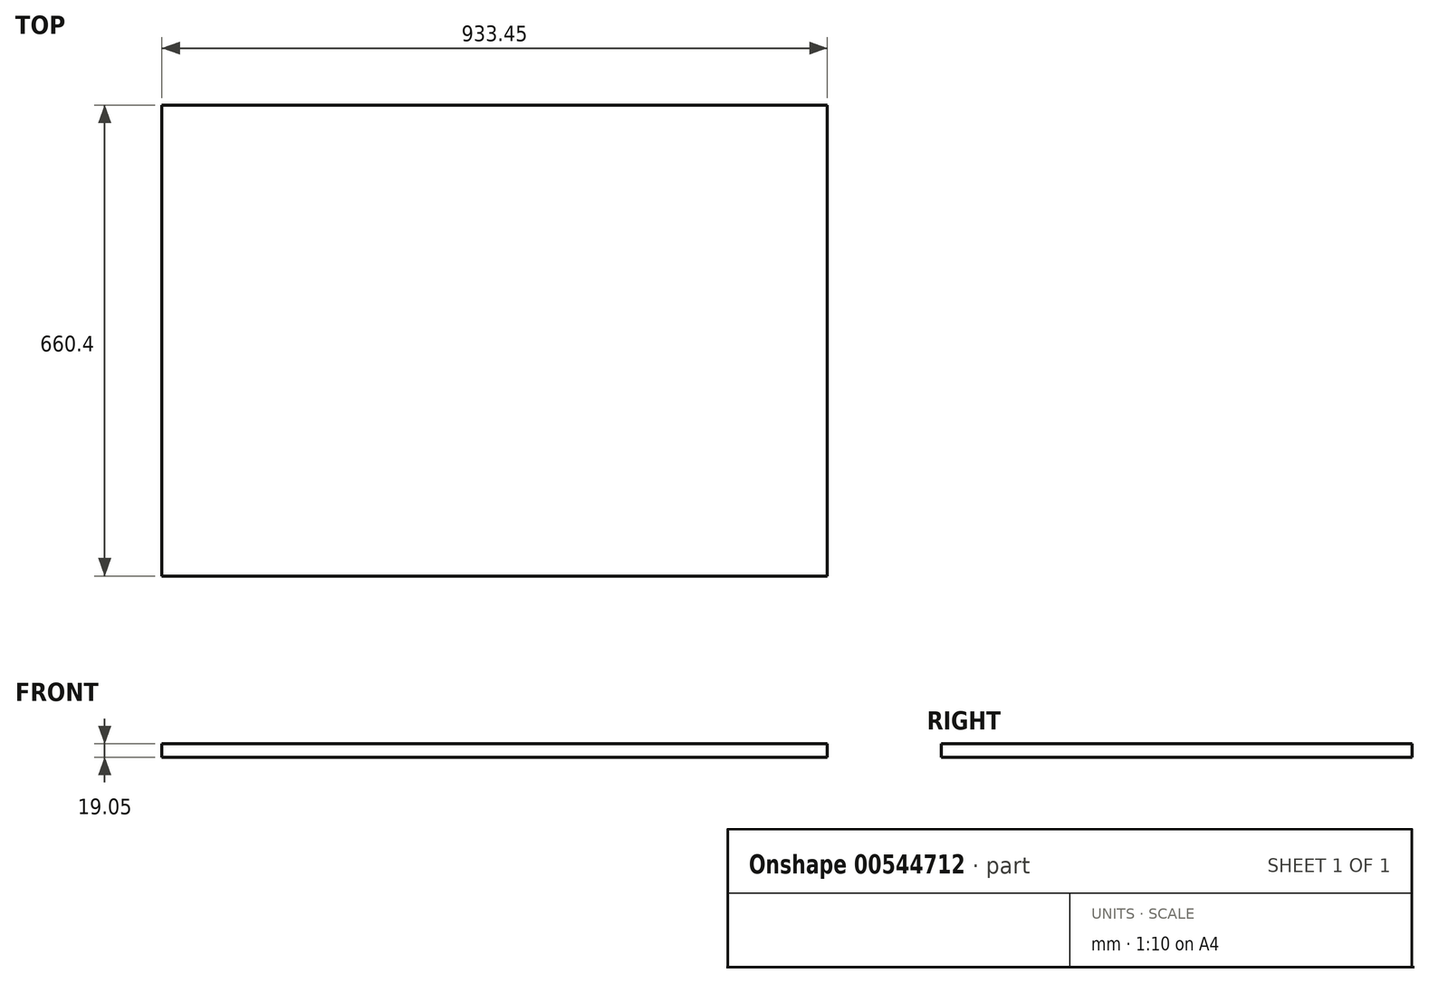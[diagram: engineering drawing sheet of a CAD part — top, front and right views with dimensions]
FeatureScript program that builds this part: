
annotation { "Feature Type Name" : "Feature", "Feature Type Description" : "" }
export const myFeature = defineFeature(function(context is Context, id is Id, definition is map)
    precondition{}
    {
        {
            var Q0;
            Q0=qCreatedBy(makeId("Top.planeOp"),FACE);
            var sketch = newSketch(context, id + "F0", { "sketchPlane" : qUnion([Q0])});
            skLineSegment(sketch, "E0.bottom", {"start": v(0, 0) * mm, "end": v(933.45, 0) * mm});
            skLineSegment(sketch, "E0.top", {"start": v(0, 660.4) * mm, "end": v(933.45, 660.4) * mm});
            skLineSegment(sketch, "E0.left", {"start": v(0, 0) * mm, "end": v(0, 660.4) * mm});
            skLineSegment(sketch, "E0.right", {"start": v(933.45, 0) * mm, "end": v(933.45, 660.4) * mm});
            skSolve(sketch);
        }
        {
            var Q0;
            Q0=makeQuery(id+"F0.imprint","IMPRINT",FACE,{"disambiguationData":[TD([[makeQuery(id+"F0.imprint","IMPRINT",EDGE,{"derivedFrom":sQuery(id+"F0.wireOp",EDGE,"E0.bottom")}),1.0]])]});
            extrude(context, id + "F1", {"entities" : qUnion([Q0]), "depth" : 19.05 * mm, "offsetDistance" : 25.4 * mm});
        }
    });
